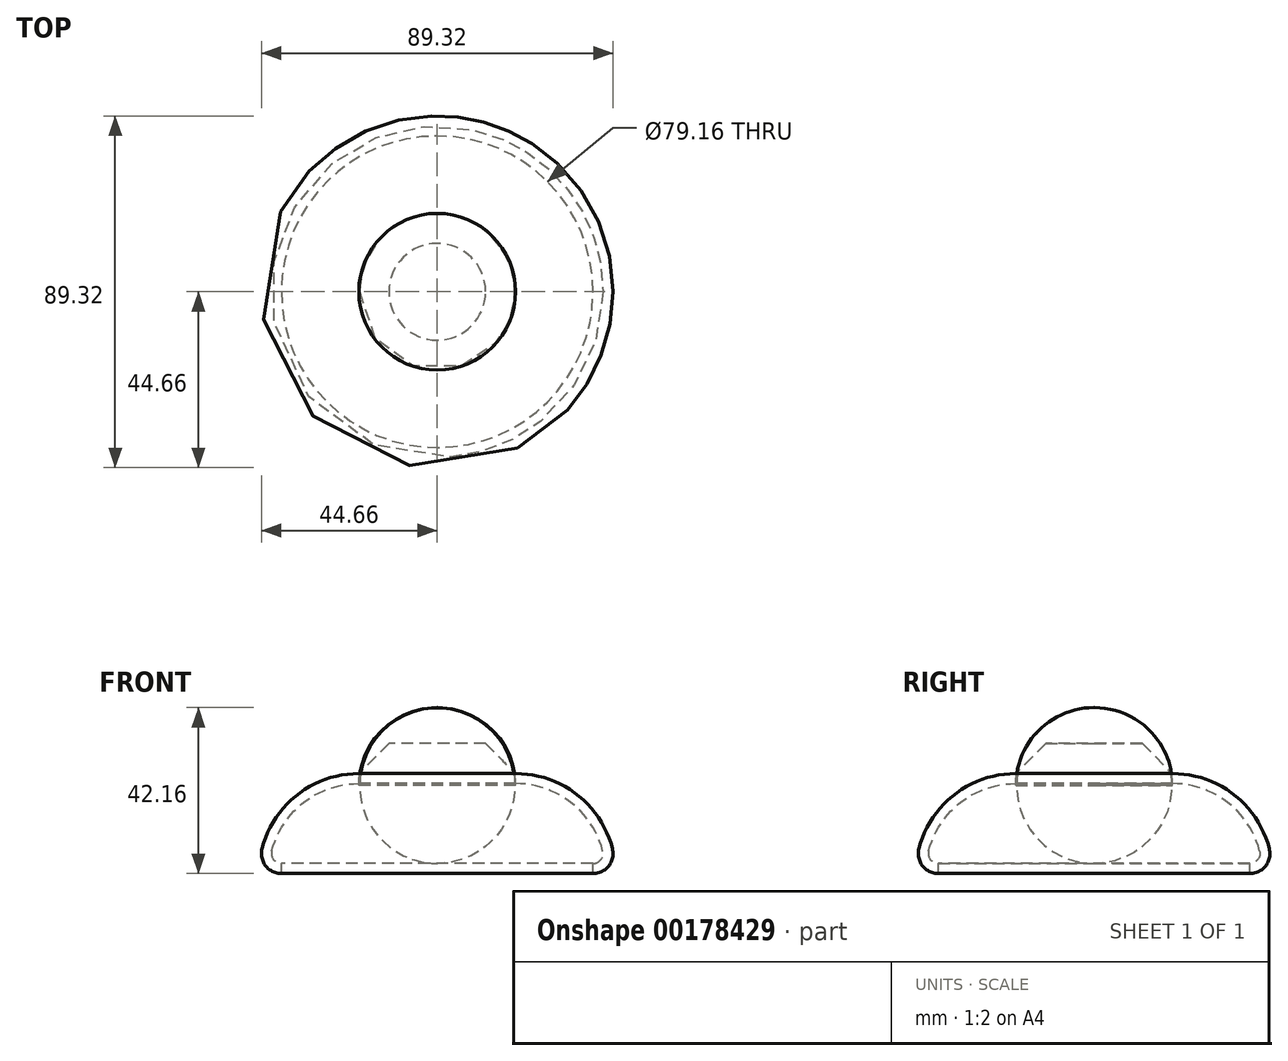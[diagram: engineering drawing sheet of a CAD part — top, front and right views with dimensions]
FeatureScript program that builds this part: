
annotation { "Feature Type Name" : "Feature", "Feature Type Description" : "" }
export const myFeature = defineFeature(function(context is Context, id is Id, definition is map)
    precondition{}
    {
        {
            var Q0;
            Q0=qCreatedBy(makeId("Top.planeOp"),FACE);
            var sketch = newSketch(context, id + "F0", { "sketchPlane" : qUnion([Q0])});
            skCircle(sketch, "E0", {"center": v(0, 0) * mm, "radius": 45.3 * mm});
            skSolve(sketch);
        }
        {
            var Q0;
            Q0=makeQuery(id+"F0.imprint","IMPRINT",FACE,{"disambiguationData":[TD([[makeQuery(id+"F0.imprint","IMPRINT",EDGE,{"derivedFrom":sQuery(id+"F0.wireOp",EDGE,"E0")}),1.0]])]});
            extrude(context, id + "F1", {"entities" : qUnion([Q0]), "depth" : 25.4 * mm});
        }
        {
            var Q0;
            Q0=makeQuery(id+"F1.opExtrude","CAP_FACE",FACE,{"disambiguationData":[OSD([sQuery(id+"F0.wireOp",EDGE,"E0")])],"isStart":false});
            fillet(context, id + "F2", {"entities" : qUnion([Q0]), "radius" : 25.4 * mm, "tangentPropagation" : true, "allowEdgeOverflow" : false});
        }
        {
            var Q0;
            Q0=makeQuery(id+"F1.opExtrude","CAP_FACE",FACE,{"disambiguationData":[OSD([sQuery(id+"F0.wireOp",EDGE,"E0")])],"isStart":true});
            fillet(context, id + "F3", {"entities" : qUnion([Q0]), "radius" : 5.08 * mm, "tangentPropagation" : true, "allowEdgeOverflow" : false});
        }
        {
            var Q0;
            Q0=makeQuery(id+"F1.opExtrude","CAP_FACE",FACE,{"disambiguationData":[OSD([sQuery(id+"F0.wireOp",EDGE,"E0")])],"isStart":true});
            shell(context, id + "F4", {"entities" : qUnion([Q0]), "thickness" : 2.54 * mm});
        }
        {
            var Q0;
            Q0=makeQuery(id+"F1.opExtrude","CAP_FACE",FACE,{"disambiguationData":[OSD([sQuery(id+"F0.wireOp",EDGE,"E0")])],"isStart":false});
            extrude(context, id + "F5", {"entities" : qUnion([Q0]), "operationType" : NewBodyOperationType.ADD, "depth" : 7.62 * mm});
        }
        {
            var Q0;
            Q0=makeQuery(id+"F5.opExtrude","CAP_FACE",FACE,{"disambiguationData":[OSD([sQuery(id+"F0.wireOp",EDGE,"E0")])],"isStart":false});
            chamfer(context, id + "F6", {"entities" : qUnion([Q0]), "width" : 7.62 * mm, "tangentPropagation" : true});
        }
        {
            var Q0;
            {var subQ0=sQuery(id+"F0.wireOp",EDGE,"E0");Q0=makeQuery(id+"F4.opShell","OFFSET_FACE",FACE,{"disambiguationData":[OSD([subQ0]),TDD([makeQuery(id+"F1.opExtrude","CAP_FACE",FACE,{"disambiguationData":[OSD([subQ0])],"isStart":false})])]});}
            extrude(context, id + "F7", {"entities" : qUnion([Q0]), "operationType" : NewBodyOperationType.ADD, "depth" : 20.32 * mm});
        }
        {
            var Q0;
            Q0=makeQuery(id+"F7.opExtrude","CAP_FACE",FACE,{"disambiguationData":[OSD([sQuery(id+"F0.wireOp",EDGE,"E0")])],"isStart":false});
            fillet(context, id + "F8", {"entities" : qUnion([Q0]), "radius" : 19.8 * mm, "tangentPropagation" : true, "allowEdgeOverflow" : false});
        }
    });
